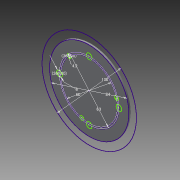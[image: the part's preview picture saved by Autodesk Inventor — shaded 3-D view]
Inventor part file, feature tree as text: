
AUTODESK INVENTOR PART (.ipt)
format: ipt  version: 2015 (Build 190159000, 159)  size: 109,568 bytes
history: native  units: mm
features: extrude x4, other x1, sketch x1
ambient origin geometry x8: Origin, YZ Plane, XZ Plane, XY Plane, X Axis, Y Axis, Z Axis, Center Point
bodies: Body1 (feature_tree)
feature tree (6):
  other  "ソリッド1"
  sketch  "スケッチ1"
  extrude  "押し出し1"  Depth=100.0mm
  extrude  "押し出し2"  Depth=63.0mm
  extrude  "押し出し3"  Depth=6.0mm
  extrude  "押し出し4"  Depth=40.0mm TaperAngle=360.0deg
